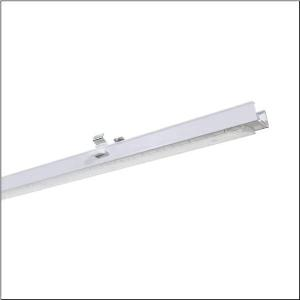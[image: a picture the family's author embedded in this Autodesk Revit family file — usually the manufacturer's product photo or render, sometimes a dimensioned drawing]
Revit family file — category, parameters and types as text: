
# Revit family: trunking_flex_31_51re12db4cb
name_source: partatom
category: Lighting Fixtures
units: mm (PartAtom-declared; Revit-internal decimal feet)

## family parameters
Cut with Voids When Loaded = No
Host = Face
Light Source = No
Part Type = Normal
Room Calculation Point = No
Round Connector Dimension = Use Diameter
Shared = No

## types (1)
- Trunking Flex 31 (1 x LED, 11500 lm, 66 W, 4000K)
    Apparent Load = 66 VA
    CIE Flux Codes = 65 91 98 99 100
    Color Rendering = 80
    Color Temperature = 4000K
    Default Elevation = 1800 mm
    Description = Trunking Flex 31, luminaire insert, of extruded aluminium section, coated, traffic white (RAL 9016), length: 1.472mm, width: 91mm, height: 53mm, LED rated luminous flux: 11.500lm, light colour: 840, control gear: DALI 2, with system connector: socket, mains connection: 220..240V, AC, 50/60Hz, rated input power: 66W, primary light control with lens, of plastic, primary optical cover: cover, of PMMA, light emission: direct distribution, protection rating (complete): IP20, insulation class (complete): insulation class I (protective earthing), certification: CE, UKCA, impact resistance: IK02, permissible ambient temperature for indoor applications: -20..+40°C, packaging unit: 1 piece
    Height = 58 mm
    Lamp = 1 x LED
    Lamp Light Flux = 11500 lm
    Lamp Power = 66 W
    Lamp count = 1
    Length = 1472 mm
    Luminous efficacy = 174 lm/W
    Manufacturer = Siteco
    ModVariant = No
    Model = 51RE12DB4CB
    Mounting Place = Ceiling
    Mounting Type = Pendant
    Number of Poles = 1
    OnlyDefault = Yes
    Power Factor = 1
    Product Name = Trunking Flex 31
    Product group = luminaire insert
    ProductGroupID = 901
    Protection Class = Protection class I
    Protection Degree = IP 20
    RLX_Detail_Level = 1
    RLX_Emergency_Light_Flux = 0 lm
    RLX_Emergency_Type = 0
    RLX_Emergency_Type_DB = No
    RlxData = <blob elided: 19541 chars, md5=c5fcea0f>
    Socket = socket
    Standby Power = 0 W
    System Light Flux = 11500 lm
    System Power = 66 W
    Type Comments = Product without accessories
    Type Image = l_1266702.jpg
    URL = http://relux.com
    VarID = ---
    Voltage = 0 V
    Weight = 0.00 kg
    Width = 65 mm

## geometry (parser evidence)
native form markers: Blend x4, Sweep x10
no freeform markers — native parametric forms only
